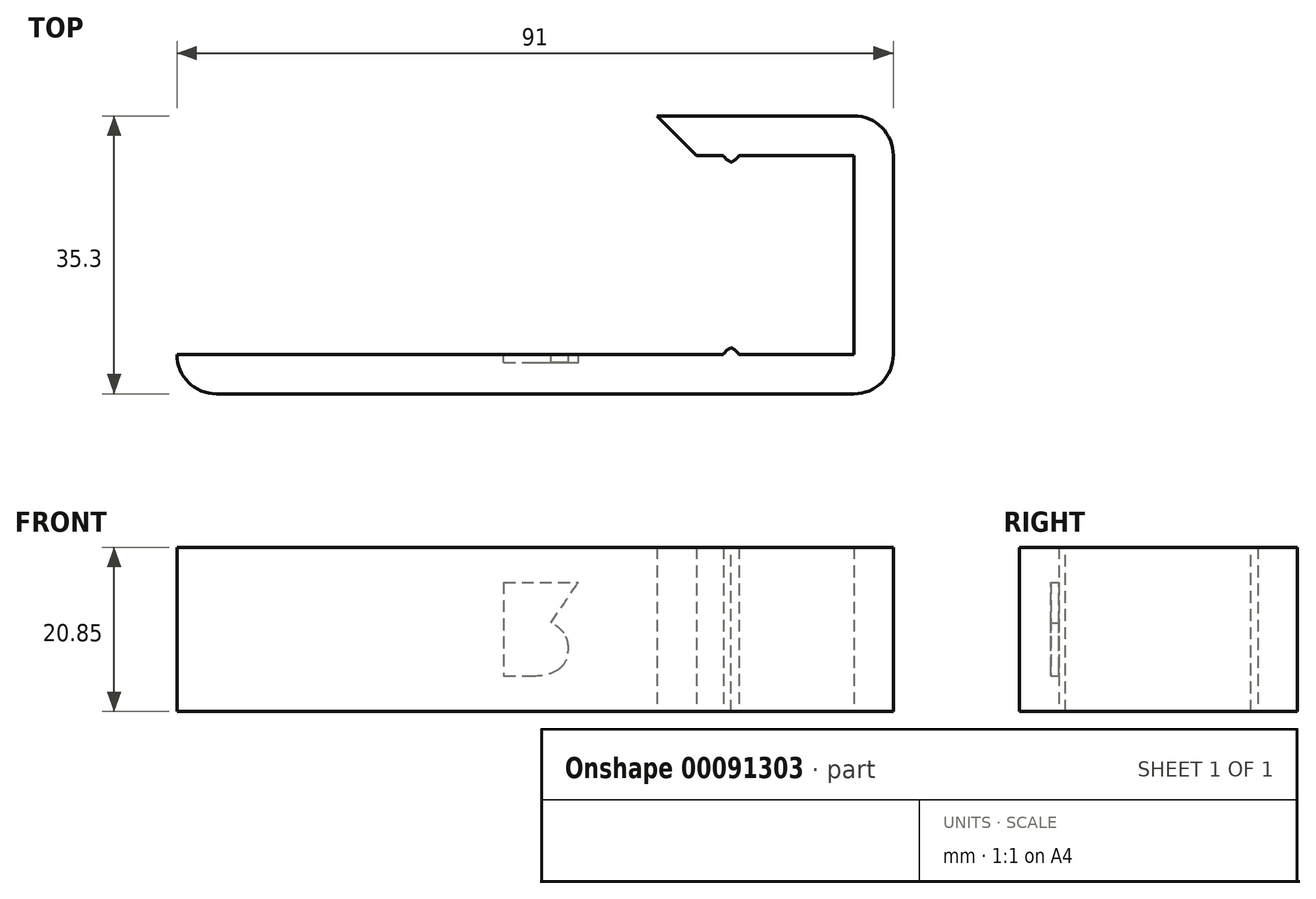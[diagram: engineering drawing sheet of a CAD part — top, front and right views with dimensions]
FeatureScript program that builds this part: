
annotation { "Feature Type Name" : "Feature", "Feature Type Description" : "" }
export const myFeature = defineFeature(function(context is Context, id is Id, definition is map)
    precondition{}
    {
        {
            var Q0;
            Q0=qCreatedBy(makeId("Top.planeOp"),FACE);
            var sketch = newSketch(context, id + "F0", { "sketchPlane" : qUnion([Q0])});
            skLineSegment(sketch, "E0", {"start": v(-86, -12.65) * mm, "end": v(0, -12.65) * mm});
            skLineSegment(sketch, "E1", {"start": v(0, -12.65) * mm, "end": v(0, 12.65) * mm});
            skLineSegment(sketch, "E2", {"start": v(0, 12.65) * mm, "end": v(-25, 12.65) * mm});
            skLineSegment(sketch, "E3.0", {"start": v(0, 17.65) * mm, "end": v(-25, 17.65) * mm});
            skLineSegment(sketch, "E3.1", {"start": v(5, -12.65) * mm, "end": v(5, 12.65) * mm});
            skLineSegment(sketch, "E3.2", {"start": v(-81, -17.65) * mm, "end": v(0, -17.65) * mm});
            skLineSegment(sketch, "E4", {"start": v(-14.6, 12.65) * mm, "end": v(-14.6, 11.65) * mm});
            skLineSegment(sketch, "E5", {"start": v(-14.6, 11.65) * mm, "end": v(-16.6, 11.65) * mm});
            skLineSegment(sketch, "E6", {"start": v(-16.6, 11.65) * mm, "end": v(-16.6, 12.65) * mm});
            skPoint(sketch, "E7", {"position": v(0, 0) * mm});
            skLineSegment(sketch, "E8", {"start": v(3.41, 0) * mm, "end": v(47.8, 0) * mm, "construction": true});
            skLineSegment(sketch, "E9.MirrorCS", {"start": v(-16.6, -11.65) * mm, "end": v(-16.6, -12.65) * mm});
            skLineSegment(sketch, "E10.MirrorCS", {"start": v(-14.6, -11.65) * mm, "end": v(-16.6, -11.65) * mm});
            skLineSegment(sketch, "E11.MirrorCS", {"start": v(-14.6, -12.65) * mm, "end": v(-14.6, -11.65) * mm});
            skPoint(sketch, "E12.visualSharp", {"position": v(5, 17.65) * mm});
            skArc(sketch, "E12.filletArc", {"start": v(5, 12.65) * mm, "mid": v(3.54, 16.19) * mm, "end": v(0, 17.65) * mm});
            skPoint(sketch, "E13.visualSharp", {"position": v(5, -17.65) * mm});
            skArc(sketch, "E13.filletArc", {"start": v(0, -17.65) * mm, "mid": v(3.54, -16.19) * mm, "end": v(5, -12.65) * mm});
            skPoint(sketch, "E14.visualSharp", {"position": v(-99.47, -17.65) * mm});
            skArc(sketch, "E14.filletArc", {"start": v(-86, -12.65) * mm, "mid": v(-84.54, -16.19) * mm, "end": v(-81, -17.65) * mm});
            skLineSegment(sketch, "E15", {"start": v(-25, 12.65) * mm, "end": v(-25, 17.65) * mm});
            skSolve(sketch);
        }
        {
            var Q0;
            Q0 = qSketchRegion(id + "F0", true);
            extrude(context, id + "F1", {"entities" : qUnion([Q0]), "depth" : (35.85 - 14 - 1) * mm});
        }
        {
            var Q0;
            Q0=makeQuery(id+"F1.opExtrude","SWEPT_EDGE",EDGE,{"disambiguationData":[OSD([sQuery(id+"F0.wireOp",EDGE,"E2"),sQuery(id+"F0.wireOp",EDGE,"E15")])]});
            chamfer(context, id + "F2", {"entities" : qUnion([Q0]), "width" : 5 * mm, "tangentPropagation" : true});
        }
        {
            var Q0;
            {var subQ0=sQuery(id+"F0.wireOp",EDGE,"E0");Q0=makeQuery(id+"F1.opExtrude","SWEPT_FACE",FACE,{"disambiguationData":[OSD([subQ0]),TDD([makeQuery(id+"F0.imprint","IMPRINT",EDGE,{"disambiguationData":[TD([[makeQuery(id+"F0.imprint","INTERSECT",VERTEX,{"derivedFrom":[subQ0,sQuery(id+"F0.wireOp",EDGE,"E14.filletArc")]}),-1.0]])],"derivedFrom":subQ0})])]});}
            var sketch = newSketch(context, id + "F3", { "sketchPlane" : qUnion([Q0])});
            skText(sketch, "E16", { "text": "R", "fontName": "OpenSans-Bold.ttf"});
            skPoint(sketch, "E17", {"position": v(46, 10.43) * mm});
            skLineSegment(sketch, "E18", {"start": v(59.34, 0) * mm, "end": v(59.34, 20.85) * mm, "construction": true});
            skPoint(sketch, "E19", {"position": v(59.34, 10.43) * mm});
            skLineSegment(sketch, "E20", {"start": v(46, 16.43) * mm, "end": v(33.92, 16.43) * mm});
            const initialGuessF3  = {"E16": [0.046, 0.01643, -1, 0, 0.012]};
            skSetInitialGuess(sketch, initialGuessF3);
            skSolve(sketch);
        }
        {
            var Q0;
            Q0=makeQuery(id+"F3.imprint","IMPRINT",FACE,{"disambiguationData":[TD([[makeQuery(id+"F3.imprint","IMPRINT",EDGE,{"derivedFrom":sQuery(id+"F3.wireOp",EDGE,"E16.sketch_text.stroke-0")}),-1.0]])]});
            var Q1;
            {var subQ0=sQuery(id+"F3.wireOp",EDGE,"E16.sketch_text.stroke-7");Q1=makeQuery(id+"F3.imprint","IMPRINT",FACE,{"disambiguationData":[TD([[makeQuery(id+"F3.imprint","IMPRINT",EDGE,{"derivedFrom":subQ0}),1.0]])]});}
            var Q2;
            Q2=makeQuery(id+"F3.imprint","IMPRINT",FACE,{"disambiguationData":[TD([[makeQuery(id+"F3.imprint","IMPRINT",EDGE,{"derivedFrom":sQuery(id+"F3.wireOp",EDGE,"E16.sketch_text.stroke-0")}),1.0]])]});
            extrude(context, id + "F4", {"entities" : qUnion([Q0, Q1, Q2]), "operationType" : NewBodyOperationType.REMOVE, "oppositeDirection" : true, "depth" : 1 * mm});
        }
        {
            var Q0;
            Q0=makeQuery(id+"F1.opExtrude","SWEPT_EDGE",EDGE,{"disambiguationData":[OSD([sQuery(id+"F0.wireOp",EDGE,"E5"),sQuery(id+"F0.wireOp",EDGE,"E6")])]});
            var Q1;
            Q1=makeQuery(id+"F1.opExtrude","SWEPT_EDGE",EDGE,{"disambiguationData":[OSD([sQuery(id+"F0.wireOp",EDGE,"E4"),sQuery(id+"F0.wireOp",EDGE,"E5")])]});
            var Q2;
            Q2=makeQuery(id+"F1.opExtrude","SWEPT_EDGE",EDGE,{"disambiguationData":[OSD([sQuery(id+"F0.wireOp",EDGE,"E9.MirrorCS"),sQuery(id+"F0.wireOp",EDGE,"E10.MirrorCS")])]});
            var Q3;
            Q3=makeQuery(id+"F1.opExtrude","SWEPT_EDGE",EDGE,{"disambiguationData":[OSD([sQuery(id+"F0.wireOp",EDGE,"E10.MirrorCS"),sQuery(id+"F0.wireOp",EDGE,"E11.MirrorCS")])]});
            fillet(context, id + "F5", {"entities" : qUnion([Q0, Q1, Q2, Q3]), "radius" : 2 * mm, "tangentPropagation" : true, "allowEdgeOverflow" : false});
        }
    });
